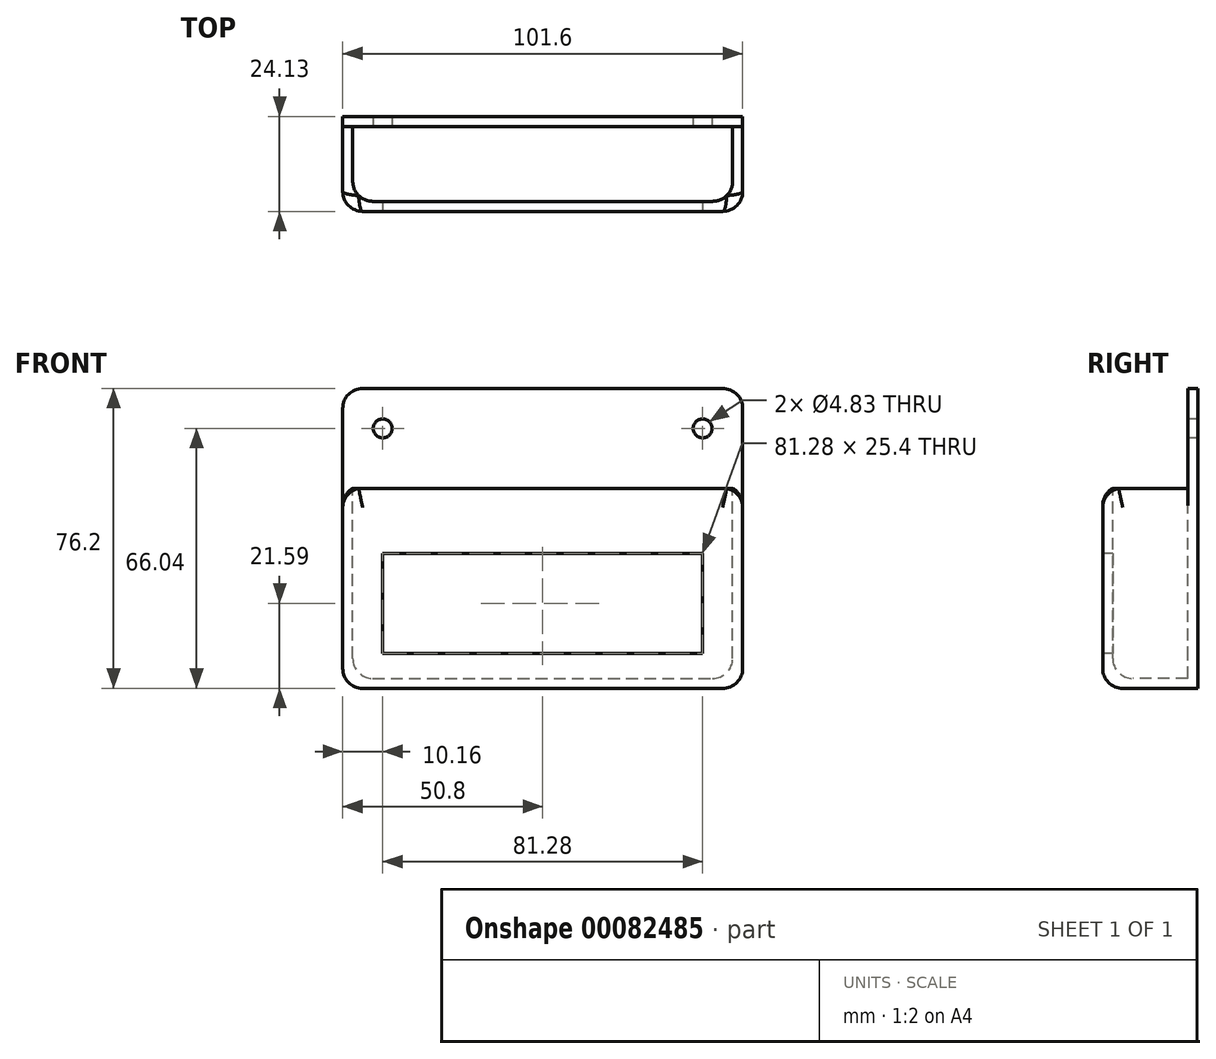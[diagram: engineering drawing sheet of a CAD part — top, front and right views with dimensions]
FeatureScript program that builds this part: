
annotation { "Feature Type Name" : "Feature", "Feature Type Description" : "" }
export const myFeature = defineFeature(function(context is Context, id is Id, definition is map)
    precondition{}
    {
        {
            var Q0;
            Q0=qCreatedBy(makeId("Front.planeOp"),FACE);
            var sketch = newSketch(context, id + "F0", { "sketchPlane" : qUnion([Q0])});
            skLineSegment(sketch, "E0.bottom", {"start": v(0, 0) * mm, "end": v(101.6, 0) * mm});
            skLineSegment(sketch, "E0.top", {"start": v(0, 76.2) * mm, "end": v(101.6, 76.2) * mm});
            skLineSegment(sketch, "E0.left", {"start": v(0, 0) * mm, "end": v(0, 76.2) * mm});
            skLineSegment(sketch, "E0.right", {"start": v(101.6, 0) * mm, "end": v(101.6, 76.2) * mm});
            skSolve(sketch);
        }
        {
            var Q0;
            Q0 = qSketchRegion(id + "F0", true);
            extrude(context, id + "F1", {"entities" : qUnion([Q0]), "depth" : 2.54 * mm});
        }
        {
            var Q0;
            Q0=makeQuery(id+"F1.opExtrude","CAP_FACE",FACE,{"disambiguationData":[OSD([sQuery(id+"F0.wireOp",EDGE,"E0.bottom"),sQuery(id+"F0.wireOp",EDGE,"E0.top"),sQuery(id+"F0.wireOp",EDGE,"E0.left"),sQuery(id+"F0.wireOp",EDGE,"E0.right")])],"isStart":false});
            var sketch = newSketch(context, id + "F2", { "sketchPlane" : qUnion([Q0])});
            skLineSegment(sketch, "E1.bottom", {"start": v(0, 50.8) * mm, "end": v(101.6, 50.8) * mm});
            skLineSegment(sketch, "E1.top", {"start": v(0, 0) * mm, "end": v(101.6, 0) * mm});
            skLineSegment(sketch, "E1.left", {"start": v(0, 50.8) * mm, "end": v(0, 0) * mm});
            skLineSegment(sketch, "E1.right", {"start": v(101.6, 50.8) * mm, "end": v(101.6, 0) * mm});
            skSolve(sketch);
        }
        {
            var Q0;
            Q0 = qSketchRegion(id + "F2", true);
            extrude(context, id + "F3", {"entities" : qUnion([Q0]), "operationType" : NewBodyOperationType.ADD, "depth" : 21.59 * mm});
        }
        {
            var Q0;
            Q0=makeQuery(id+"F1.opExtrude","SWEPT_EDGE",EDGE,{"disambiguationData":[OSD([sQuery(id+"F0.wireOp",EDGE,"E0.top"),sQuery(id+"F0.wireOp",EDGE,"E0.right")])]});
            var Q1;
            Q1=makeQuery(id+"F3.boolean.opBoolean","MERGE",EDGE,{"derivedFrom":[makeQuery(id+"F1.opExtrude","SWEPT_EDGE",EDGE,{"disambiguationData":[OSD([sQuery(id+"F0.wireOp",EDGE,"E0.bottom"),sQuery(id+"F0.wireOp",EDGE,"E0.right")])]}),makeQuery(id+"F3.opExtrude","SWEPT_EDGE",EDGE,{"disambiguationData":[OSD([sQuery(id+"F2.wireOp",EDGE,"E1.top"),sQuery(id+"F2.wireOp",EDGE,"E1.right")])]})]});
            var Q2;
            Q2=makeQuery(id+"F3.boolean.opBoolean","MERGE",EDGE,{"derivedFrom":[makeQuery(id+"F1.opExtrude","SWEPT_EDGE",EDGE,{"disambiguationData":[OSD([sQuery(id+"F0.wireOp",EDGE,"E0.bottom"),sQuery(id+"F0.wireOp",EDGE,"E0.left")])]}),makeQuery(id+"F3.opExtrude","SWEPT_EDGE",EDGE,{"disambiguationData":[OSD([sQuery(id+"F2.wireOp",EDGE,"E1.top"),sQuery(id+"F2.wireOp",EDGE,"E1.left")])]})]});
            var Q3;
            Q3=makeQuery(id+"F1.opExtrude","SWEPT_EDGE",EDGE,{"disambiguationData":[OSD([sQuery(id+"F0.wireOp",EDGE,"E0.top"),sQuery(id+"F0.wireOp",EDGE,"E0.left")])]});
            fillet(context, id + "F4", {"entities" : qUnion([Q0, Q1, Q2, Q3]), "radius" : 5.08 * mm, "tangentPropagation" : true, "allowEdgeOverflow" : false});
        }
        {
            var Q0;
            Q0=makeQuery(id+"F3.opExtrude","SWEPT_FACE",FACE,{"disambiguationData":[OSD([sQuery(id+"F2.wireOp",EDGE,"E1.bottom")])]});
            var sketch = newSketch(context, id + "F5", { "sketchPlane" : qUnion([Q0])});
            skLineSegment(sketch, "E2.bottom", {"start": v(2.54, -2.54) * mm, "end": v(99.06, -2.54) * mm});
            skLineSegment(sketch, "E2.top", {"start": v(2.54, -21.59) * mm, "end": v(99.06, -21.59) * mm});
            skLineSegment(sketch, "E2.left", {"start": v(2.54, -2.54) * mm, "end": v(2.54, -21.59) * mm});
            skLineSegment(sketch, "E2.right", {"start": v(99.06, -2.54) * mm, "end": v(99.06, -21.59) * mm});
            skSolve(sketch);
        }
        {
            var Q0;
            Q0 = qSketchRegion(id + "F5", true);
            extrude(context, id + "F6", {"entities" : qUnion([Q0]), "operationType" : NewBodyOperationType.REMOVE, "oppositeDirection" : true, "depth" : 48.26 * mm});
        }
        {
            var Q0;
            Q0=makeQuery(id+"F3.opExtrude","CAP_EDGE",EDGE,{"disambiguationData":[OSD([sQuery(id+"F2.wireOp",EDGE,"E1.right")])],"isStart":false});
            fillet(context, id + "F7", {"entities" : qUnion([Q0]), "radius" : 5.08 * mm, "tangentPropagation" : true, "allowEdgeOverflow" : false});
        }
        {
            var Q0;
            Q0=makeQuery(id+"F6.boolean.opBoolean","COPY",EDGE,{"derivedFrom":makeQuery(id+"F6.opExtrude","SWEPT_EDGE",EDGE,{"disambiguationData":[OSD([sQuery(id+"F5.wireOp",EDGE,"E2.top"),sQuery(id+"F5.wireOp",EDGE,"E2.right")])]})});
            fillet(context, id + "F8", {"entities" : qUnion([Q0]), "radius" : 5.08 * mm, "tangentPropagation" : true, "allowEdgeOverflow" : false});
        }
        {
            var Q0;
            Q0=makeQuery(id+"F6.boolean.opBoolean","COPY",EDGE,{"derivedFrom":makeQuery(id+"F6.opExtrude","SWEPT_EDGE",EDGE,{"disambiguationData":[OSD([sQuery(id+"F5.wireOp",EDGE,"E2.top"),sQuery(id+"F5.wireOp",EDGE,"E2.left")])]})});
            fillet(context, id + "F9", {"entities" : qUnion([Q0]), "radius" : 5.08 * mm, "tangentPropagation" : true, "allowEdgeOverflow" : false});
        }
        {
            var Q0;
            Q0=makeQuery(id+"F6.boolean.opBoolean","COPY",EDGE,{"derivedFrom":makeQuery(id+"F6.opExtrude","CAP_EDGE",EDGE,{"disambiguationData":[OSD([sQuery(id+"F5.wireOp",EDGE,"E2.left")])],"isStart":false})});
            var Q1;
            Q1=makeQuery(id+"F6.boolean.opBoolean","COPY",EDGE,{"derivedFrom":makeQuery(id+"F6.opExtrude","CAP_EDGE",EDGE,{"disambiguationData":[OSD([sQuery(id+"F5.wireOp",EDGE,"E2.left")])],"isStart":true})});
            var Q2;
            Q2=makeQuery(id+"F3.opExtrude","SWEPT_EDGE",EDGE,{"disambiguationData":[OSD([sQuery(id+"F0.wireOp",EDGE,"E0.left"),sQuery(id+"F2.wireOp",EDGE,"E1.bottom"),sQuery(id+"F2.wireOp",EDGE,"E1.left")])]});
            var Q3;
            {var subQ0=sQuery(id+"F2.wireOp",EDGE,"E1.top");var subQ1=sQuery(id+"F0.wireOp",EDGE,"E0.bottom");Q3=makeQuery(id+"F4.opFillet","BLEND_EDGE",EDGE,{"blendedFrom":[makeQuery(id+"F3.boolean.opBoolean","MERGE",EDGE,{"derivedFrom":[makeQuery(id+"F1.opExtrude","SWEPT_EDGE",EDGE,{"disambiguationData":[OSD([subQ1,sQuery(id+"F0.wireOp",EDGE,"E0.right")])]}),makeQuery(id+"F3.opExtrude","SWEPT_EDGE",EDGE,{"disambiguationData":[OSD([subQ0,sQuery(id+"F2.wireOp",EDGE,"E1.right")])]})]}),makeQuery(id+"F3.boolean.opBoolean","MERGE",FACE,{"derivedFrom":[makeQuery(id+"F1.opExtrude","SWEPT_FACE",FACE,{"disambiguationData":[OSD([subQ1])]}),makeQuery(id+"F3.opExtrude","SWEPT_FACE",FACE,{"disambiguationData":[OSD([subQ0])]})]})],"blendedInto":[makeQuery(id+"F3.boolean.opBoolean","MERGE",FACE,{"derivedFrom":[makeQuery(id+"F1.opExtrude","SWEPT_FACE",FACE,{"disambiguationData":[OSD([subQ1])]}),makeQuery(id+"F3.opExtrude","SWEPT_FACE",FACE,{"disambiguationData":[OSD([subQ0])]})]})]});}
            fillet(context, id + "F10", {"entities" : qUnion([Q0, Q1, Q2, Q3]), "radius" : 5.08 * mm, "tangentPropagation" : true, "allowEdgeOverflow" : false});
        }
        {
            var Q0;
            Q0=makeQuery(id+"F3.opExtrude","CAP_FACE",FACE,{"disambiguationData":[OSD([sQuery(id+"F2.wireOp",EDGE,"E1.bottom"),sQuery(id+"F2.wireOp",EDGE,"E1.top"),sQuery(id+"F2.wireOp",EDGE,"E1.left"),sQuery(id+"F2.wireOp",EDGE,"E1.right")])],"isStart":false});
            var sketch = newSketch(context, id + "F11", { "sketchPlane" : qUnion([Q0])});
            skLineSegment(sketch, "E3.bottom", {"start": v(10.16, 34.3) * mm, "end": v(91.44, 34.3) * mm});
            skLineSegment(sketch, "E3.top", {"start": v(10.16, 8.9) * mm, "end": v(91.44, 8.9) * mm});
            skLineSegment(sketch, "E3.left", {"start": v(10.16, 34.3) * mm, "end": v(10.16, 8.9) * mm});
            skLineSegment(sketch, "E3.right", {"start": v(91.44, 34.3) * mm, "end": v(91.44, 8.9) * mm});
            skSolve(sketch);
        }
        {
            var Q0;
            Q0 = qSketchRegion(id + "F11", true);
            var Q1;
            Q1=makeQuery(id+"F6.boolean.opBoolean","MERGE",FACE,{"derivedFrom":[makeQuery(id+"F1.opExtrude","CAP_FACE",FACE,{"disambiguationData":[OSD([sQuery(id+"F0.wireOp",EDGE,"E0.bottom"),sQuery(id+"F0.wireOp",EDGE,"E0.top"),sQuery(id+"F0.wireOp",EDGE,"E0.left"),sQuery(id+"F0.wireOp",EDGE,"E0.right")])],"isStart":false}),makeQuery(id+"F6.opExtrude","SWEPT_FACE",FACE,{"disambiguationData":[OSD([sQuery(id+"F5.wireOp",EDGE,"E2.bottom")])]})]});
            extrude(context, id + "F12", {"entities" : qUnion([Q0]), "operationType" : NewBodyOperationType.REMOVE, "endBound" : BoundingType.UP_TO_SURFACE, "oppositeDirection" : true, "endBoundEntityFace" : qUnion([Q1]), "depth" : 25.4 * mm});
        }
        {
            var Q0;
            Q0=makeQuery(id+"F6.boolean.opBoolean","MERGE",FACE,{"derivedFrom":[makeQuery(id+"F1.opExtrude","CAP_FACE",FACE,{"disambiguationData":[OSD([sQuery(id+"F0.wireOp",EDGE,"E0.bottom"),sQuery(id+"F0.wireOp",EDGE,"E0.top"),sQuery(id+"F0.wireOp",EDGE,"E0.left"),sQuery(id+"F0.wireOp",EDGE,"E0.right")])],"isStart":false}),makeQuery(id+"F6.opExtrude","SWEPT_FACE",FACE,{"disambiguationData":[OSD([sQuery(id+"F5.wireOp",EDGE,"E2.bottom")])]})]});
            var sketch = newSketch(context, id + "F13", { "sketchPlane" : qUnion([Q0])});
            skCircle(sketch, "E4", {"center": v(91.44, 66.04) * mm, "radius": 2.41 * mm});
            skCircle(sketch, "E5", {"center": v(10.16, 66.04) * mm, "radius": 2.41 * mm});
            skSolve(sketch);
        }
        {
            var Q0;
            Q0 = qSketchRegion(id + "F13", true);
            extrude(context, id + "F14", {"entities" : qUnion([Q0]), "operationType" : NewBodyOperationType.REMOVE, "endBound" : BoundingType.THROUGH_ALL, "oppositeDirection" : true, "depth" : 25.4 * mm});
        }
    });
